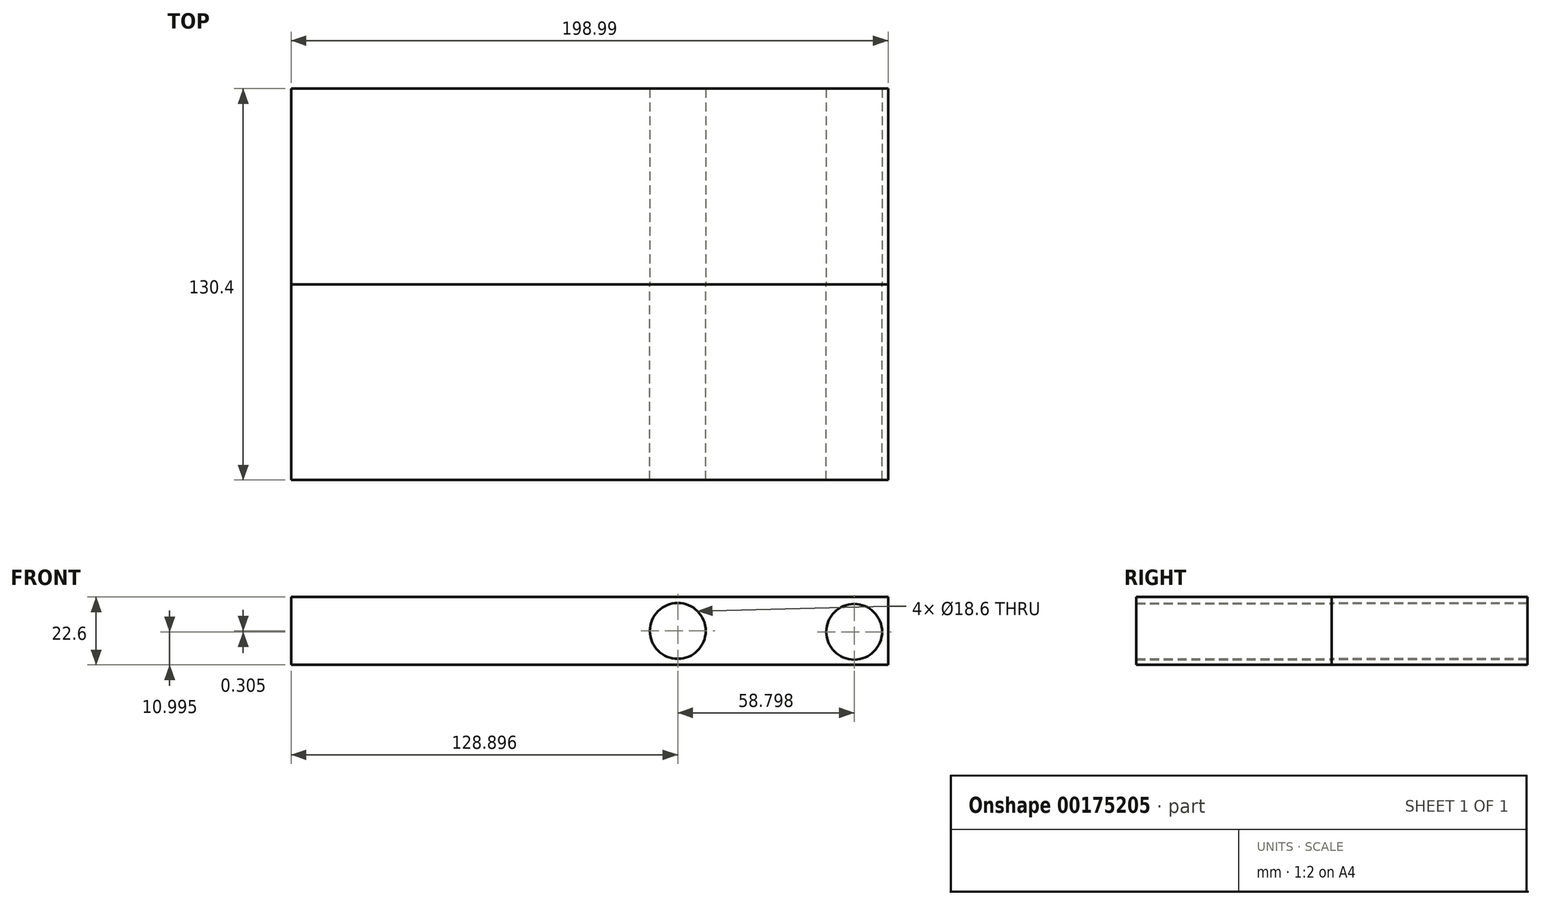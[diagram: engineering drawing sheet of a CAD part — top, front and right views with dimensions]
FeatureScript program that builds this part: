
annotation { "Feature Type Name" : "Feature", "Feature Type Description" : "" }
export const myFeature = defineFeature(function(context is Context, id is Id, definition is map)
    precondition{}
    {
        {
            var Q0;
            Q0=qCreatedBy(makeId("Front.planeOp"),FACE);
            var sketch = newSketch(context, id + "F0", { "sketchPlane" : qUnion([Q0])});
            skCircle(sketch, "E0", {"center": v(-52.63, 11.3) * mm, "radius": 9.3 * mm});
            skLineSegment(sketch, "E1", {"start": v(-63.93, 11.3) * mm, "end": v(135.06, 11.3) * mm, "construction": true});
            skCircle(sketch, "E2", {"center": v(-33.03, 11.3) * mm, "radius": 9.3 * mm});
            skCircle(sketch, "E3", {"center": v(-13.43, 11.3) * mm, "radius": 9.3 * mm});
            skCircle(sketch, "E4", {"center": v(6.17, 11.3) * mm, "radius": 9.3 * mm});
            skCircle(sketch, "E5", {"center": v(25.77, 11.3) * mm, "radius": 9.3 * mm});
            skLineSegment(sketch, "E6.bottom", {"start": v(-63.93, 0) * mm, "end": v(135.06, 0) * mm});
            skLineSegment(sketch, "E6.top", {"start": v(-63.93, 22.6) * mm, "end": v(135.06, 22.6) * mm});
            skLineSegment(sketch, "E6.left", {"start": v(-63.93, 0) * mm, "end": v(-63.93, 22.6) * mm});
            skLineSegment(sketch, "E6.right", {"start": v(135.06, 0) * mm, "end": v(135.06, 22.6) * mm});
            skLineSegment(sketch, "E7", {"start": v(-63.93, 11.3) * mm, "end": v(-61.93, 11.3) * mm});
            skLineSegment(sketch, "E8", {"start": v(-61.93, 11.3) * mm, "end": v(135.06, 11.3) * mm});
            skCircle(sketch, "E9", {"center": v(45.37, 11.3) * mm, "radius": 9.3 * mm});
            skCircle(sketch, "E10", {"center": v(64.97, 11.3) * mm, "radius": 9.3 * mm});
            skCircle(sketch, "E11", {"center": v(84.57, 11.3) * mm, "radius": 9.3 * mm});
            skCircle(sketch, "E12", {"center": v(104.17, 11.3) * mm, "radius": 9.3 * mm});
            skCircle(sketch, "E13", {"center": v(123.76, 11) * mm, "radius": 9.3 * mm});
            skSolve(sketch);
        }
        {
            var Q0;
            Q0=makeQuery(id+"F0.imprint","IMPRINT",FACE,{"disambiguationData":[TD([[makeQuery(id+"F0.imprint","IMPRINT",EDGE,{"derivedFrom":sQuery(id+"F0.wireOp",EDGE,"E0")}),1.0]])]});
            var Q1;
            Q1=makeQuery(id+"F0.imprint","IMPRINT",FACE,{"disambiguationData":[TD([[makeQuery(id+"F0.imprint","IMPRINT",EDGE,{"derivedFrom":sQuery(id+"F0.wireOp",EDGE,"E2")}),1.0]])]});
            var Q2;
            Q2=makeQuery(id+"F0.imprint","IMPRINT",FACE,{"disambiguationData":[TD([[makeQuery(id+"F0.imprint","IMPRINT",EDGE,{"derivedFrom":sQuery(id+"F0.wireOp",EDGE,"E3")}),1.0]])]});
            var Q3;
            Q3=makeQuery(id+"F0.imprint","IMPRINT",FACE,{"disambiguationData":[TD([[makeQuery(id+"F0.imprint","IMPRINT",EDGE,{"derivedFrom":sQuery(id+"F0.wireOp",EDGE,"E4")}),1.0]])]});
            var Q4;
            Q4=makeQuery(id+"F0.imprint","IMPRINT",FACE,{"disambiguationData":[TD([[makeQuery(id+"F0.imprint","IMPRINT",EDGE,{"derivedFrom":sQuery(id+"F0.wireOp",EDGE,"E5")}),1.0]])]});
            var Q5;
            {var subQ0=sQuery(id+"F0.wireOp",EDGE,"E9");var subQ1=sQuery(id+"F0.wireOp",EDGE,"E8");var subQ2=makeQuery(id+"F0.imprint","INTERSECT",VERTEX,{"disambiguationData":[OD(0.0)],"derivedFrom":[subQ1,subQ0]});Q5=makeQuery(id+"F0.imprint","IMPRINT",FACE,{"disambiguationData":[TD([[makeQuery(id+"F0.imprint","IMPRINT",EDGE,{"disambiguationData":[TD([[subQ2,-1.0]])],"derivedFrom":subQ1}),-1.0]])]});}
            var Q6;
            {var subQ0=sQuery(id+"F0.wireOp",EDGE,"E10");var subQ1=sQuery(id+"F0.wireOp",EDGE,"E8");var subQ2=makeQuery(id+"F0.imprint","INTERSECT",VERTEX,{"disambiguationData":[OD(0.0)],"derivedFrom":[subQ1,subQ0]});Q6=makeQuery(id+"F0.imprint","IMPRINT",FACE,{"disambiguationData":[TD([[makeQuery(id+"F0.imprint","IMPRINT",EDGE,{"disambiguationData":[TD([[subQ2,-1.0]])],"derivedFrom":subQ1}),-1.0]])]});}
            var Q7;
            {var subQ0=sQuery(id+"F0.wireOp",EDGE,"E9");var subQ1=sQuery(id+"F0.wireOp",EDGE,"E8");var subQ2=makeQuery(id+"F0.imprint","INTERSECT",VERTEX,{"disambiguationData":[OD(0.0)],"derivedFrom":[subQ1,subQ0]});Q7=makeQuery(id+"F0.imprint","IMPRINT",FACE,{"disambiguationData":[TD([[makeQuery(id+"F0.imprint","IMPRINT",EDGE,{"disambiguationData":[TD([[subQ2,-1.0]])],"derivedFrom":subQ1}),1.0]])]});}
            var Q8;
            {var subQ0=sQuery(id+"F0.wireOp",EDGE,"E10");var subQ1=sQuery(id+"F0.wireOp",EDGE,"E8");var subQ2=makeQuery(id+"F0.imprint","INTERSECT",VERTEX,{"disambiguationData":[OD(0.0)],"derivedFrom":[subQ1,subQ0]});Q8=makeQuery(id+"F0.imprint","IMPRINT",FACE,{"disambiguationData":[TD([[makeQuery(id+"F0.imprint","IMPRINT",EDGE,{"disambiguationData":[TD([[subQ2,-1.0]])],"derivedFrom":subQ1}),1.0]])]});}
            var Q9;
            {var subQ0=sQuery(id+"F0.wireOp",EDGE,"E11");var subQ1=sQuery(id+"F0.wireOp",EDGE,"E8");var subQ2=makeQuery(id+"F0.imprint","INTERSECT",VERTEX,{"disambiguationData":[OD(0.0)],"derivedFrom":[subQ1,subQ0]});Q9=makeQuery(id+"F0.imprint","IMPRINT",FACE,{"disambiguationData":[TD([[makeQuery(id+"F0.imprint","IMPRINT",EDGE,{"disambiguationData":[TD([[subQ2,-1.0]])],"derivedFrom":subQ1}),-1.0]])]});}
            var Q10;
            {var subQ0=sQuery(id+"F0.wireOp",EDGE,"E11");var subQ1=sQuery(id+"F0.wireOp",EDGE,"E8");var subQ2=makeQuery(id+"F0.imprint","INTERSECT",VERTEX,{"disambiguationData":[OD(0.0)],"derivedFrom":[subQ1,subQ0]});Q10=makeQuery(id+"F0.imprint","IMPRINT",FACE,{"disambiguationData":[TD([[makeQuery(id+"F0.imprint","IMPRINT",EDGE,{"disambiguationData":[TD([[subQ2,-1.0]])],"derivedFrom":subQ1}),1.0]])]});}
            var Q11;
            {var subQ0=sQuery(id+"F0.wireOp",EDGE,"E12");var subQ1=sQuery(id+"F0.wireOp",EDGE,"E8");var subQ2=makeQuery(id+"F0.imprint","INTERSECT",VERTEX,{"disambiguationData":[OD(0.0)],"derivedFrom":[subQ1,subQ0]});Q11=makeQuery(id+"F0.imprint","IMPRINT",FACE,{"disambiguationData":[TD([[makeQuery(id+"F0.imprint","IMPRINT",EDGE,{"disambiguationData":[TD([[subQ2,-1.0]])],"derivedFrom":subQ1}),-1.0]])]});}
            var Q12;
            {var subQ0=sQuery(id+"F0.wireOp",EDGE,"E12");var subQ1=sQuery(id+"F0.wireOp",EDGE,"E8");var subQ2=makeQuery(id+"F0.imprint","INTERSECT",VERTEX,{"disambiguationData":[OD(0.0)],"derivedFrom":[subQ1,subQ0]});Q12=makeQuery(id+"F0.imprint","IMPRINT",FACE,{"disambiguationData":[TD([[makeQuery(id+"F0.imprint","IMPRINT",EDGE,{"disambiguationData":[TD([[subQ2,-1.0]])],"derivedFrom":subQ1}),1.0]])]});}
            var Q13;
            {var subQ0=sQuery(id+"F0.wireOp",EDGE,"E13");var subQ1=sQuery(id+"F0.wireOp",EDGE,"E8");var subQ2=makeQuery(id+"F0.imprint","INTERSECT",VERTEX,{"disambiguationData":[OD(0.0)],"derivedFrom":[subQ1,subQ0]});Q13=makeQuery(id+"F0.imprint","IMPRINT",FACE,{"disambiguationData":[TD([[makeQuery(id+"F0.imprint","IMPRINT",EDGE,{"disambiguationData":[TD([[subQ2,-1.0]])],"derivedFrom":subQ1}),-1.0]])]});}
            var Q14;
            {var subQ0=sQuery(id+"F0.wireOp",EDGE,"E13");var subQ1=sQuery(id+"F0.wireOp",EDGE,"E8");var subQ2=makeQuery(id+"F0.imprint","INTERSECT",VERTEX,{"disambiguationData":[OD(0.0)],"derivedFrom":[subQ1,subQ0]});Q14=makeQuery(id+"F0.imprint","IMPRINT",FACE,{"disambiguationData":[TD([[makeQuery(id+"F0.imprint","IMPRINT",EDGE,{"disambiguationData":[TD([[subQ2,-1.0]])],"derivedFrom":subQ1}),1.0]])]});}
            extrude(context, id + "F1", {"entities" : qUnion([Q0, Q1, Q2, Q3, Q4, Q5, Q6, Q7, Q8, Q9, Q10, Q11, Q12, Q13, Q14]), "depth" : 65.2 * mm});
        }
        {
            var Q0;
            Q0=makeQuery(id+"F1.opExtrude","SWEPT_BODY",BODY,{"disambiguationData":[OSD([sQuery(id+"F0.wireOp",EDGE,"E0")])]});
            var Q1;
            Q1=makeQuery(id+"F1.opExtrude","SWEPT_BODY",BODY,{"disambiguationData":[OSD([sQuery(id+"F0.wireOp",EDGE,"E2")])]});
            var Q2;
            Q2=makeQuery(id+"F1.opExtrude","SWEPT_BODY",BODY,{"disambiguationData":[OSD([sQuery(id+"F0.wireOp",EDGE,"E3")])]});
            var Q3;
            Q3=makeQuery(id+"F1.opExtrude","SWEPT_BODY",BODY,{"disambiguationData":[OSD([sQuery(id+"F0.wireOp",EDGE,"E4")])]});
            var Q4;
            Q4=makeQuery(id+"F1.opExtrude","SWEPT_BODY",BODY,{"disambiguationData":[OSD([sQuery(id+"F0.wireOp",EDGE,"E5")])]});
            var Q5;
            Q5=makeQuery(id+"F1.opExtrude","SWEPT_BODY",BODY,{"disambiguationData":[OSD([sQuery(id+"F0.wireOp",EDGE,"9f00e928-39c8-4f2f-9055-81cdd0864639")])]});
            var Q6;
            Q6=makeQuery(id+"F1.opExtrude","SWEPT_BODY",BODY,{"disambiguationData":[OSD([sQuery(id+"F0.wireOp",EDGE,"E9")])]});
            var Q7;
            Q7=makeQuery(id+"F1.opExtrude","SWEPT_BODY",BODY,{"disambiguationData":[OSD([sQuery(id+"F0.wireOp",EDGE,"E10")])]});
            var Q8;
            Q8=makeQuery(id+"F1.opExtrude","SWEPT_BODY",BODY,{"disambiguationData":[OSD([sQuery(id+"F0.wireOp",EDGE,"E11")])]});
            var Q9;
            Q9=makeQuery(id+"F1.opExtrude","SWEPT_BODY",BODY,{"disambiguationData":[OSD([sQuery(id+"F0.wireOp",EDGE,"E12")])]});
            var Q10;
            Q10=makeQuery(id+"F1.opExtrude","SWEPT_BODY",BODY,{"disambiguationData":[OSD([sQuery(id+"F0.wireOp",EDGE,"E13")])]});
            var Q11;
            Q11=qCreatedBy(makeId("Front.planeOp"),FACE);
            mirror(context, id + "F2", {"entities" : qUnion([Q0, Q1, Q2, Q3, Q4, Q5, Q6, Q7, Q8, Q9, Q10]), "mirrorPlane" : qUnion([Q11])});
        }
    });
